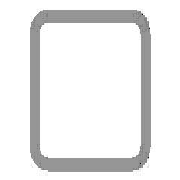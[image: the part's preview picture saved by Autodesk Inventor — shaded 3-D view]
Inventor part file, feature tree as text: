
AUTODESK INVENTOR PART (.ipt)
format: ipt  version: 2024 (Build 280153000, 153)  size: 135,168 bytes
history: native  units: mm (DEFAULTED — no unit token found)
features: other x4, plane x2, extrude x1, split x1, sketch x1
ambient origin geometry x8: Origin, YZ Plane, XZ Plane, XY Plane, X Axis, Y Axis, Z Axis, Center Point
bodies: Solid1 (feature_tree)
feature tree (9):
  parser-record x1  (decoder bookkeeping rows leaked as tree rows — omitted from the tree; the rows remain in map.json)
  other  "Driven Length"
  other  "Plano inicial"
  other  "Plano final"
  extrude  "Cuerpo"  TaperAngle=0.0deg  [1 undecoded]
  plane  "Plano de trabajo4"
  split  "Dividir1"
  sketch  "Sketch3"  dims[d3=374.6mm d4=0.0mm d10=50.8mm d11=50.8mm d12=3.175mm d13=25.4mm d14=400.0mm d15=25.4mm d16=25.4mm d17=6.35mm d18=90.0deg d19=374.6mm]
  plane  "Work Plane3"
note: 1 required parameter value undecoded (feature->parameter linkage not recoverable at this tier; creation-order binding heuristic only, values carry confidence <= 0.55)
